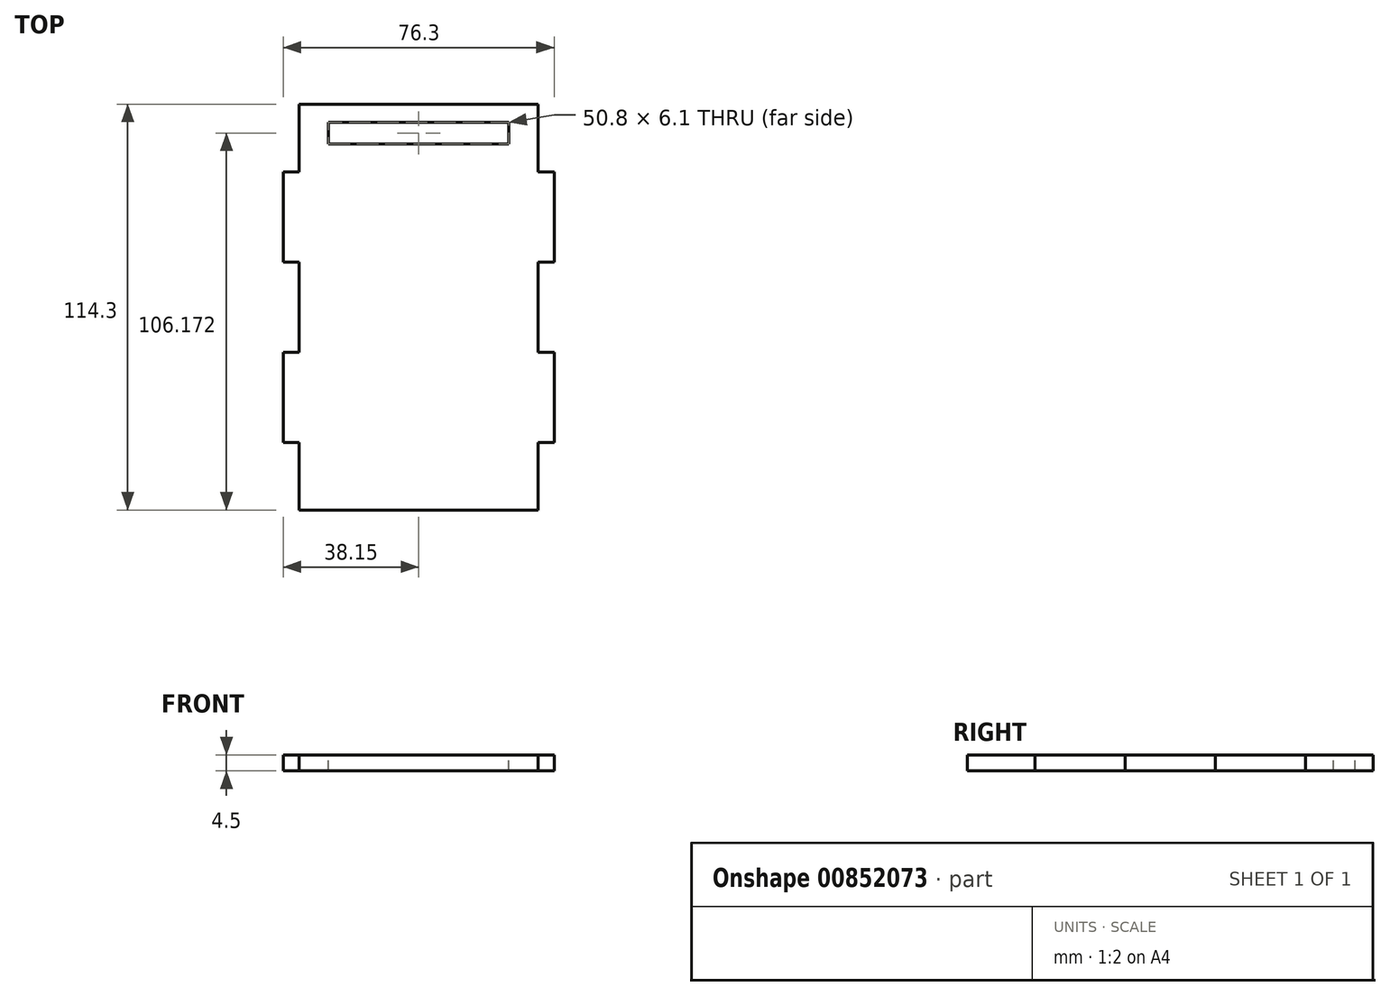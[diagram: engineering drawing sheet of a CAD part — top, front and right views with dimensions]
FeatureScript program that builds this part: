
annotation { "Feature Type Name" : "Feature", "Feature Type Description" : "" }
export const myFeature = defineFeature(function(context is Context, id is Id, definition is map)
    precondition{}
    {
        {
            var Q0;
            Q0=qCreatedBy(makeId("Top.planeOp"),FACE);
            var sketch = newSketch(context, id + "F0", { "sketchPlane" : qUnion([Q0])});
            skLineSegment(sketch, "E0.bottom", {"start": v(-33.66, 57.15) * mm, "end": v(33.65, 57.15) * mm});
            skLineSegment(sketch, "E0.top", {"start": v(-33.66, -57.15) * mm, "end": v(33.66, -57.15) * mm});
            skLineSegment(sketch, "E0.left", {"start": v(-33.66, 57.15) * mm, "end": v(-33.66, -57.15) * mm, "construction": true});
            skLineSegment(sketch, "E0.right", {"start": v(33.66, 57.15) * mm, "end": v(33.66, -57.15) * mm, "construction": true});
            skLineSegment(sketch, "E1", {"start": v(-33.66, 0) * mm, "end": v(33.66, 0) * mm, "construction": true});
            skLineSegment(sketch, "E2", {"start": v(-33.66, 57.15) * mm, "end": v(-33.66, 38.1) * mm});
            skLineSegment(sketch, "E3", {"start": v(-33.65, 38.1) * mm, "end": v(-38.15, 38.1) * mm});
            skLineSegment(sketch, "E4", {"start": v(-38.15, 38.1) * mm, "end": v(-38.15, 12.7) * mm});
            skLineSegment(sketch, "E5", {"start": v(-38.15, 12.7) * mm, "end": v(-33.65, 12.7) * mm});
            skLineSegment(sketch, "E6", {"start": v(-33.66, 12.7) * mm, "end": v(-33.66, 0) * mm});
            skLineSegment(sketch, "E7.MirrorCS", {"start": v(-38.15, -12.7) * mm, "end": v(-33.65, -12.7) * mm});
            skLineSegment(sketch, "E8.MirrorCS", {"start": v(-33.65, -38.1) * mm, "end": v(-38.15, -38.1) * mm});
            skLineSegment(sketch, "E9.MirrorCS", {"start": v(-38.15, -38.1) * mm, "end": v(-38.15, -12.7) * mm});
            skLineSegment(sketch, "E10.MirrorCS", {"start": v(-33.66, -12.7) * mm, "end": v(-33.66, 0) * mm});
            skLineSegment(sketch, "E11.MirrorCS", {"start": v(-33.66, -57.15) * mm, "end": v(-33.66, -38.1) * mm});
            skLineSegment(sketch, "E12.MirrorCS", {"start": v(38.15, -12.7) * mm, "end": v(33.65, -12.7) * mm});
            skLineSegment(sketch, "E13.MirrorCS", {"start": v(33.65, -38.1) * mm, "end": v(38.15, -38.1) * mm});
            skLineSegment(sketch, "E14.MirrorCS", {"start": v(38.15, 12.7) * mm, "end": v(33.65, 12.7) * mm});
            skLineSegment(sketch, "E15.MirrorCS", {"start": v(33.65, 38.1) * mm, "end": v(38.15, 38.1) * mm});
            skLineSegment(sketch, "E16.MirrorCS", {"start": v(33.66, -12.7) * mm, "end": v(33.66, 0) * mm});
            skLineSegment(sketch, "E17.MirrorCS", {"start": v(33.66, 57.15) * mm, "end": v(33.66, 38.1) * mm});
            skLineSegment(sketch, "E18.MirrorCS", {"start": v(33.66, 12.7) * mm, "end": v(33.66, 0) * mm});
            skLineSegment(sketch, "E19.MirrorCS", {"start": v(33.66, -57.15) * mm, "end": v(33.66, -38.1) * mm});
            skLineSegment(sketch, "E20.MirrorCS", {"start": v(38.15, -38.1) * mm, "end": v(38.15, -12.7) * mm});
            skLineSegment(sketch, "E21.MirrorCS", {"start": v(38.15, 38.1) * mm, "end": v(38.15, 12.7) * mm});
            skSolve(sketch);
        }
        {
            var Q0;
            Q0 = qSketchRegion(id + "F0", true);
            extrude(context, id + "F1", {"entities" : qUnion([Q0]), "depth" : 4.5 * mm, "offsetDistance" : 25.4 * mm});
        }
        {
            var Q0;
            Q0=makeQuery(id+"F1.opExtrude","CAP_FACE",FACE,{"disambiguationData":[OSD([sQuery(id+"F0.wireOp",EDGE,"E0.bottom"),sQuery(id+"F0.wireOp",EDGE,"E0.top"),sQuery(id+"F0.wireOp",EDGE,"E2"),sQuery(id+"F0.wireOp",EDGE,"E3"),sQuery(id+"F0.wireOp",EDGE,"E4"),sQuery(id+"F0.wireOp",EDGE,"E5"),sQuery(id+"F0.wireOp",EDGE,"E6"),sQuery(id+"F0.wireOp",EDGE,"E7.MirrorCS"),sQuery(id+"F0.wireOp",EDGE,"E8.MirrorCS"),sQuery(id+"F0.wireOp",EDGE,"E9.MirrorCS"),sQuery(id+"F0.wireOp",EDGE,"E10.MirrorCS"),sQuery(id+"F0.wireOp",EDGE,"E11.MirrorCS"),sQuery(id+"F0.wireOp",EDGE,"E12.MirrorCS"),sQuery(id+"F0.wireOp",EDGE,"E13.MirrorCS"),sQuery(id+"F0.wireOp",EDGE,"E14.MirrorCS"),sQuery(id+"F0.wireOp",EDGE,"E15.MirrorCS"),sQuery(id+"F0.wireOp",EDGE,"E16.MirrorCS"),sQuery(id+"F0.wireOp",EDGE,"E17.MirrorCS"),sQuery(id+"F0.wireOp",EDGE,"E18.MirrorCS"),sQuery(id+"F0.wireOp",EDGE,"E19.MirrorCS"),sQuery(id+"F0.wireOp",EDGE,"E20.MirrorCS"),sQuery(id+"F0.wireOp",EDGE,"E21.MirrorCS")])],"isStart":false});
            var sketch = newSketch(context, id + "F2", { "sketchPlane" : qUnion([Q0])});
            skLineSegment(sketch, "E22.bottom", {"start": v(-25.4, 52.07) * mm, "end": v(25.4, 52.07) * mm});
            skLineSegment(sketch, "E22.top", {"start": v(-25.4, 45.97) * mm, "end": v(-9.53, 45.97) * mm});
            skLineSegment(sketch, "E22.left", {"start": v(-25.4, 52.07) * mm, "end": v(-25.4, 45.97) * mm});
            skLineSegment(sketch, "E22.right", {"start": v(25.4, 52.07) * mm, "end": v(25.4, 45.97) * mm});
            skLineSegment(sketch, "E23", {"start": v(0, 52.07) * mm, "end": v(0, 0) * mm, "construction": true});
            skPoint(sketch, "E23.endSnap0", {"position": v(0, -57.15) * mm});
            skLineSegment(sketch, "E24.top", {"start": v(-9.53, 20.57) * mm, "end": v(9.53, 20.57) * mm, "construction": true});
            skLineSegment(sketch, "E24.left", {"start": v(-9.53, 45.97) * mm, "end": v(-9.53, 45.97) * mm});
            skLineSegment(sketch, "E25", {"start": v(-9.53, 45.97) * mm, "end": v(-9.53, 20.57) * mm, "construction": true});
            skLineSegment(sketch, "E26", {"start": v(9.52, 45.97) * mm, "end": v(25.4, 45.97) * mm});
            skLineSegment(sketch, "E27", {"start": v(-9.53, 45.97) * mm, "end": v(9.52, 45.97) * mm});
            skLineSegment(sketch, "E28", {"start": v(9.52, 45.97) * mm, "end": v(9.53, 20.57) * mm, "construction": true});
            skSolve(sketch);
        }
        {
            var Q0;
            Q0 = qSketchRegion(id + "F2", true);
            extrude(context, id + "F3", {"entities" : qUnion([Q0]), "operationType" : NewBodyOperationType.REMOVE, "endBound" : BoundingType.THROUGH_ALL, "oppositeDirection" : true, "depth" : 25.4 * mm, "offsetDistance" : 25.4 * mm});
        }
    });
